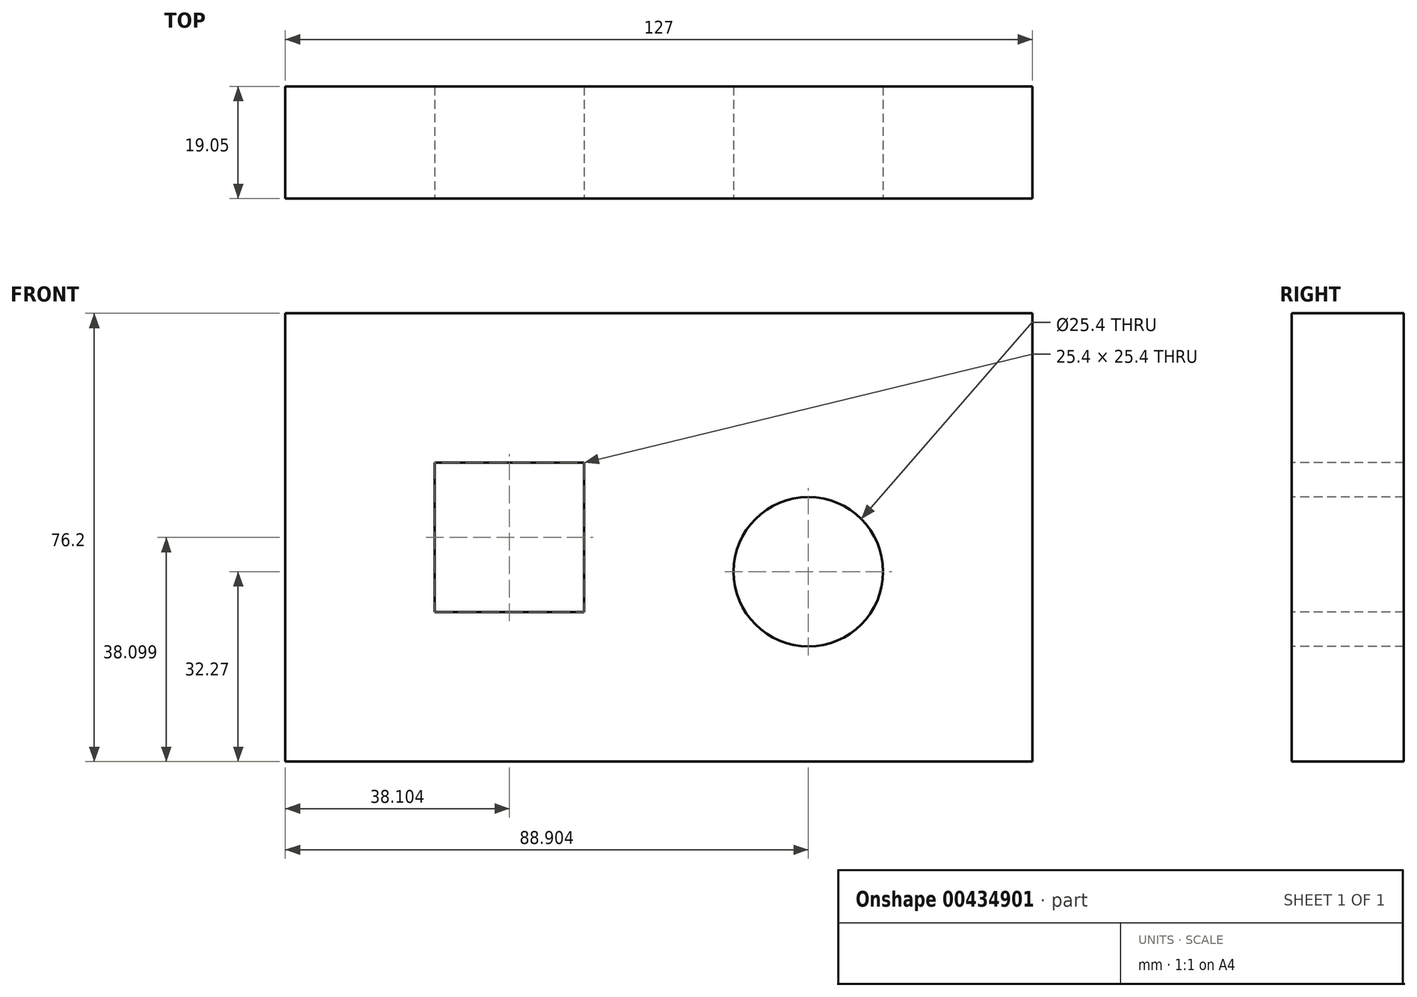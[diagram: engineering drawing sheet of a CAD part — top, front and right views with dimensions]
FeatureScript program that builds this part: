
annotation { "Feature Type Name" : "Feature", "Feature Type Description" : "" }
export const myFeature = defineFeature(function(context is Context, id is Id, definition is map)
    precondition{}
    {
        {
            var Q0;
            Q0=qCreatedBy(makeId("Front.planeOp"),FACE);
            var sketch = newSketch(context, id + "F0", { "sketchPlane" : qUnion([Q0])});
            skLineSegment(sketch, "E0", {"start": v(-69.13, -32.27) * mm, "end": v(57.87, -32.27) * mm});
            skLineSegment(sketch, "E1", {"start": v(57.87, -32.27) * mm, "end": v(57.87, 43.93) * mm});
            skLineSegment(sketch, "E2", {"start": v(57.87, 43.93) * mm, "end": v(-69.13, 43.93) * mm});
            skLineSegment(sketch, "E3", {"start": v(-69.13, 43.93) * mm, "end": v(-69.13, -32.27) * mm});
            skSolve(sketch);
        }
        {
            var Q0;
            Q0 = qSketchRegion(id + "F0", true);
            extrude(context, id + "F1", {"entities" : qUnion([Q0]), "depth" : 19.05 * mm});
        }
        {
            var Q0;
            Q0=makeQuery(id+"F1.opExtrude","CAP_FACE",FACE,{"disambiguationData":[OSD([sQuery(id+"F0.wireOp",EDGE,"E0"),sQuery(id+"F0.wireOp",EDGE,"E1"),sQuery(id+"F0.wireOp",EDGE,"E2"),sQuery(id+"F0.wireOp",EDGE,"E3")])],"isStart":false});
            var sketch = newSketch(context, id + "F2", { "sketchPlane" : qUnion([Q0])});
            skLineSegment(sketch, "E4.bottom", {"start": v(-18.33, -6.87) * mm, "end": v(-43.73, -6.87) * mm});
            skLineSegment(sketch, "E4.top", {"start": v(-18.33, 18.53) * mm, "end": v(-43.73, 18.53) * mm});
            skLineSegment(sketch, "E4.left", {"start": v(-18.33, -6.87) * mm, "end": v(-18.33, 18.53) * mm});
            skLineSegment(sketch, "E4.right", {"start": v(-43.73, -6.87) * mm, "end": v(-43.73, 18.53) * mm});
            skPoint(sketch, "E4.middle", {"position": v(-31.03, 5.83) * mm});
            skSolve(sketch);
        }
        {
            var Q0;
            Q0 = qSketchRegion(id + "F2", true);
            extrude(context, id + "F3", {"entities" : qUnion([Q0]), "operationType" : NewBodyOperationType.REMOVE, "oppositeDirection" : true, "depth" : 19.05 * mm});
        }
        {
            var Q0;
            Q0=makeQuery(id+"F1.opExtrude","CAP_FACE",FACE,{"disambiguationData":[OSD([sQuery(id+"F0.wireOp",EDGE,"E0"),sQuery(id+"F0.wireOp",EDGE,"E1"),sQuery(id+"F0.wireOp",EDGE,"E2"),sQuery(id+"F0.wireOp",EDGE,"E3")])],"isStart":false});
            var sketch = newSketch(context, id + "F4", { "sketchPlane" : qUnion([Q0])});
            skCircle(sketch, "E5", {"center": v(19.77, 0) * mm, "radius": 12.7 * mm});
            skSolve(sketch);
        }
        {
            var Q0;
            Q0 = qSketchRegion(id + "F4", true);
            extrude(context, id + "F5", {"entities" : qUnion([Q0]), "operationType" : NewBodyOperationType.REMOVE, "oppositeDirection" : true, "depth" : 19.05 * mm});
        }
    });
